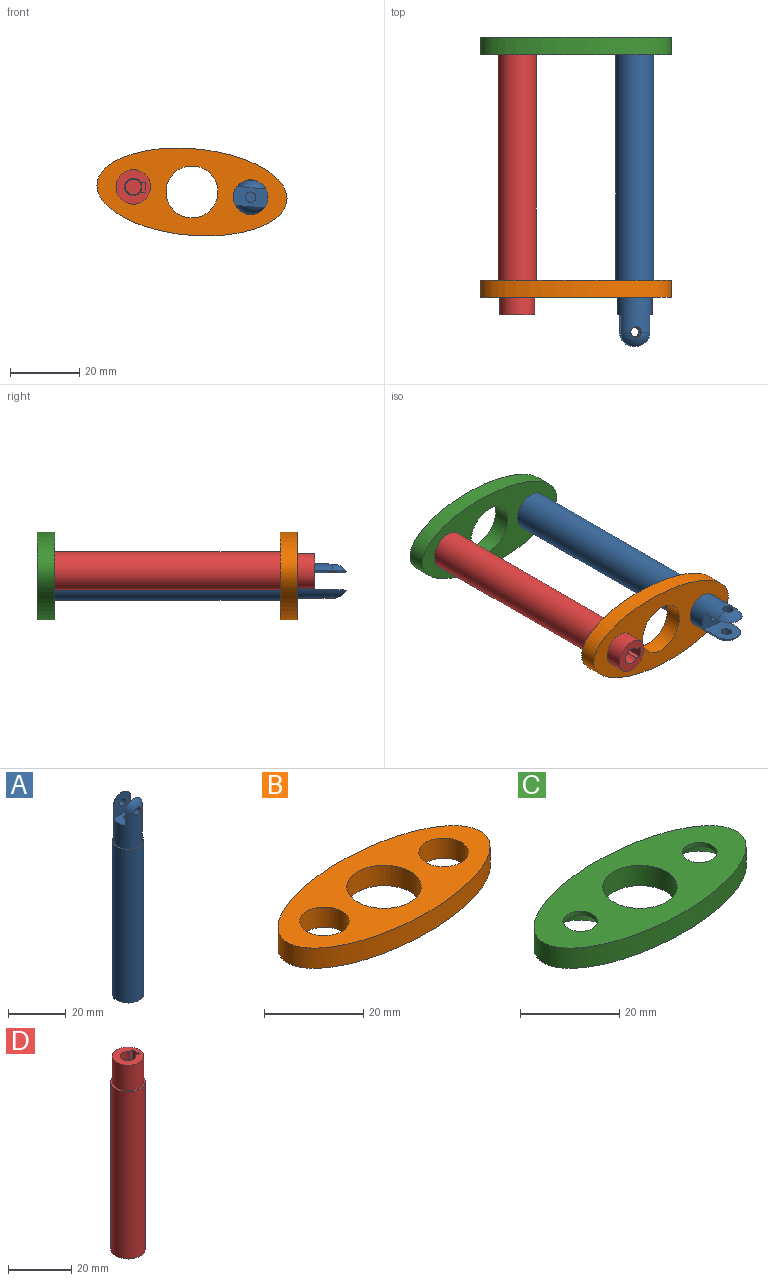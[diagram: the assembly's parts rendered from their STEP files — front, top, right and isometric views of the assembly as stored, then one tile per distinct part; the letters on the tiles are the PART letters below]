
ASSEMBLY  parts=4 mates=8
PART A: 15 faces, bbox 11x11x84.2 mm
  f0: sphere r=5mm, area 31.7mm2, adj f4,f7,f10
  f1: cylinder r=5.5mm len=65mm, axis (0,0,-1), area 2246.2mm2, adj f2,f3
  f2: plane 11x11mm, normal (0,0,1), area 16.5mm2, adj f1,f4
  f3: plane 11x11mm, normal (0,0,-1), area 75.4mm2, adj f1,f14
  f4: cylinder r=5mm len=15mm, axis (0,0,-1), area 405.9mm2, adj f0,f2,f5,f6,f7,f8,f9,f10
  f5: sphere r=5mm, area 31.7mm2, adj f4,f8,f9
  f6: plane 10x5.5mm, normal (0,0,1), area 45mm2, adj f4,f7,f8,f11
  f7: plane 9.18x8.35mm, normal (0,1,0), area 62.1mm2, adj f0,f4,f6,f10
  f8: plane 9.18x8.35mm, normal (0,-1,0), area 62.1mm2, adj f4,f5,f6,f9
  f9: cylinder r=1.5mm len=3mm, axis (0,-1,0), area 19.6mm2, adj f4,f5,f8
  f10: cylinder r=1.5mm len=3mm, axis (0,-1,0), area 19.6mm2, adj f0,f4,f7
  f11: cylinder r=1.5mm len=40mm, axis (0,0,1), area 377mm2, adj f6,f12
  f12: plane 3x3mm, normal (0,0,1), area 7.1mm2, adj f11
  f13: cone r=0mm half-angle=59deg, axis (0,0,-1), area 22.9mm2, adj f14
  f14: cylinder r=2.5mm len=15mm, axis (0,0,-1), area 235.6mm2, adj f3,f13
PART B: 6 faces, bbox 55x25x5 mm
  f0: cylinder r=7.5mm len=15mm, axis (0,0,-1), area 235.6mm2, adj f4,f5
  f1: cylinder r=5mm len=10mm, axis (0,0,-1), area 157.1mm2, adj f4,f5
  f2: cylinder r=5mm len=10mm, axis (0,0,-1), area 157.1mm2, adj f4,f5
  f3: extruded ~55x25mm, area 650.7mm2, adj f4,f5
  f4: plane 55x25mm, normal (0,0,1), area 746.1mm2, adj f0,f1,f2,f3
  f5: plane 55x25mm, normal (0,0,-1), area 746.1mm2, adj f0,f1,f2,f3
PART C: 8 faces, bbox 55x25x5 mm
  f0: cylinder r=7.5mm len=15mm, axis (0,0,-1), area 235.6mm2, adj f4,f5
  f1: cylinder r=3.5mm len=7mm, axis (0,0,-1), area 22mm2, adj f4,f6
  f2: cylinder r=3.5mm len=7mm, axis (0,0,-1), area 22mm2, adj f4,f7
  f3: extruded ~55x25mm, area 650.7mm2, adj f4,f5
  f4: plane 55x25mm, normal (0,0,1), area 826.2mm2, adj f0,f1,f2,f3
  f5: plane 55x25mm, normal (0,0,-1), area 549.8mm2, adj f0,f3,f6,f7
  f6: cone r=7.5mm half-angle=45deg, axis (0,0,-1), area 195.5mm2, adj f1,f5
  f7: cone r=7.5mm half-angle=45deg, axis (0,0,-1), area 195.5mm2, adj f2,f5
PART D: 15 faces, bbox 11x11x75 mm
  f0: plane 10x10mm, normal (0,0,1), area 55.4mm2, adj f4,f7,f11,f12,f13
  f1: cylinder r=5.5mm len=65mm, axis (0,0,-1), area 2246.2mm2, adj f2,f3
  f2: plane 11x11mm, normal (0,0,1), area 16.5mm2, adj f1,f4
  f3: plane 11x11mm, normal (0,0,-1), area 75.4mm2, adj f1,f6
  f4: cylinder r=5mm len=10mm, axis (0,0,-1), area 314.2mm2, adj f0,f2
  f5: cone r=0mm half-angle=59deg, axis (0,0,-1), area 22.9mm2, adj f6
  f6: cylinder r=2.5mm len=15mm, axis (0,0,-1), area 235.6mm2, adj f3,f5
  f7: cylinder r=2.5mm len=11mm, axis (0,0,1), area 143.8mm2, adj f0,f8,f11,f12,f14
  f8: plane 5x5mm, normal (0,0,1), area 3.7mm2, adj f7,f10
  f9: plane 4.5x4.5mm, normal (0,0,1), area 15.9mm2, adj f10
  f10: cylinder r=2.25mm len=24mm, axis (0,0,1), area 339.3mm2, adj f8,f9
  f11: plane 9x1.5mm, normal (0,-1,0), area 13.5mm2, adj f0,f7,f13,f14
  f12: plane 9x1.5mm, normal (0,1,0), area 13.5mm2, adj f0,f7,f13,f14
  f13: plane 9x3mm, normal (-1,0,0), area 27mm2, adj f0,f11,f12,f14
  f14: plane 3x1.5mm, normal (0,0,1), area 3.5mm2, adj f7,f11,f12,f13
PLACE A rot(axis=(1,0.04,-0.04),90.1deg) t=(17,-5,0)mm
PLACE B rot(axis=(1,0.04,-0.04),90.1deg) t=(0.07,-70,1.49)mm
PLACE C rot(axis=(1,0.04,-0.04),90.1deg) t=(0.07,0,1.49)mm
PLACE D rot(axis=(1,0.04,-0.04),90.1deg) t=(-16.87,-5,2.99)mm
MATE cylindrical A.f4 <-> B.f2  axis (0,1,0) through (17,-77.5,0)mm
MATE cylindrical B.f1 <-> D.f4  axis (0,1,0) through (-16.87,-70,2.99)mm
MATE planar C.f0 <-> A.f1  axis (0,-1,0) through (0.07,-5,1.49)mm
MATE planar D.f1 <-> C.f0  axis (0,1,0) through (-16.87,-5,2.99)mm
MATE parallel D.f11 <-> A.f8  axis (-0.09,0,-1) through (-14,-75.5,4.24)mm
MATE cylindrical C.f1 <-> A.f13  axis (0,1,0) through (17,-4.5,0)mm
MATE planar D.f5 <-> B.f0  axis (0,-1,0) through (-16.87,-70,2.99)mm
MATE cylindrical D.f5 <-> C.f2  axis (0,1,0) through (-16.87,-12.5,2.99)mm
